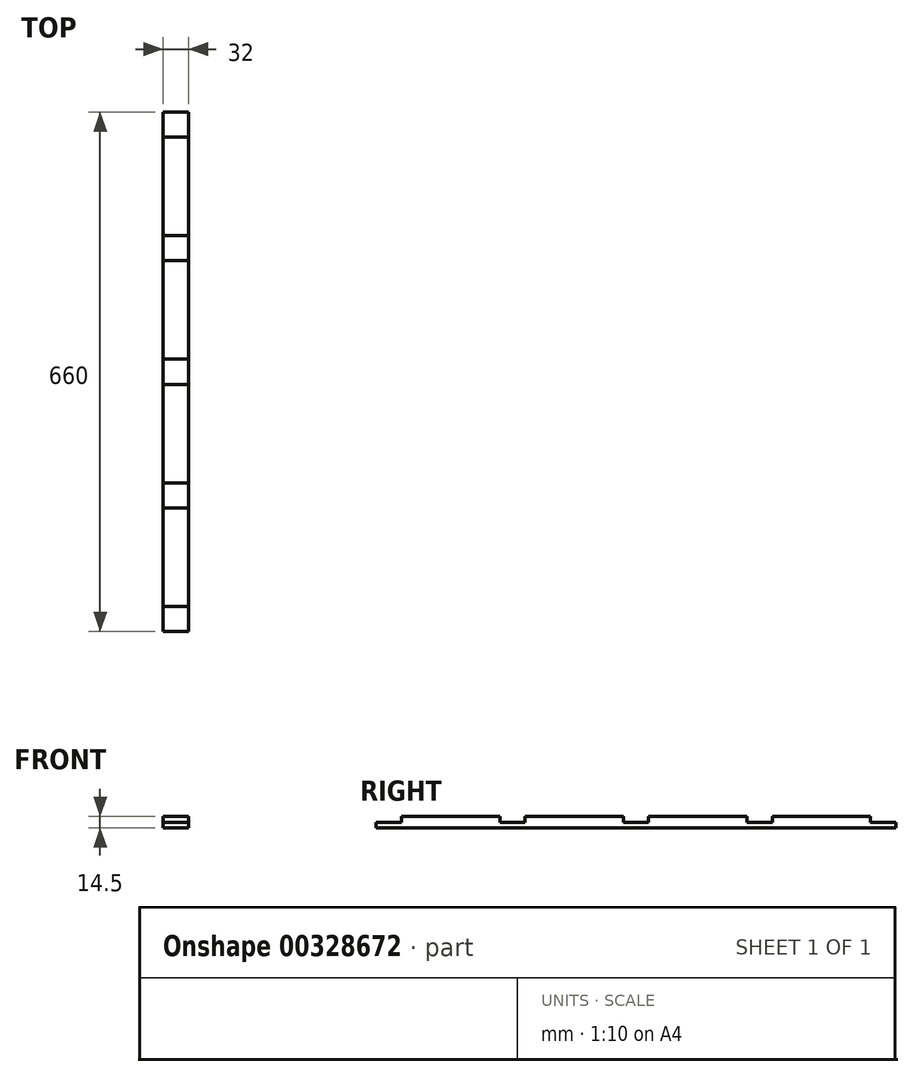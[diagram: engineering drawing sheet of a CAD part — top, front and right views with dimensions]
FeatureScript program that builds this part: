
annotation { "Feature Type Name" : "Feature", "Feature Type Description" : "" }
export const myFeature = defineFeature(function(context is Context, id is Id, definition is map)
    precondition{}
    {
        {
            var Q0;
            Q0=qCreatedBy(makeId("Right.planeOp"),FACE);
            var sketch = newSketch(context, id + "F0", { "sketchPlane" : qUnion([Q0])});
            skLineSegment(sketch, "E0.bottom", {"start": v(0, 0) * mm, "end": v(660, 0) * mm});
            skLineSegment(sketch, "E0.top", {"start": v(32, 14.5) * mm, "end": v(157, 14.5) * mm});
            skLineSegment(sketch, "E0.left", {"start": v(0, 0) * mm, "end": v(0, 7.25) * mm});
            skLineSegment(sketch, "E0.right", {"start": v(660, 0) * mm, "end": v(660, 7.25) * mm});
            skLineSegment(sketch, "E1", {"start": v(0, 7.25) * mm, "end": v(32, 7.25) * mm});
            skLineSegment(sketch, "E2", {"start": v(32, 7.25) * mm, "end": v(32, 14.5) * mm});
            skPoint(sketch, "E3.orphan", {"position": v(0, 14.5) * mm});
            skLineSegment(sketch, "E4", {"start": v(157, 14.5) * mm, "end": v(157, 7.25) * mm});
            skLineSegment(sketch, "E5", {"start": v(157, 7.25) * mm, "end": v(189, 7.25) * mm});
            skLineSegment(sketch, "E6", {"start": v(189, 7.25) * mm, "end": v(189, 14.5) * mm});
            skLineSegment(sketch, "E7.trimOffspring", {"start": v(189, 14.5) * mm, "end": v(314, 14.5) * mm});
            skLineSegment(sketch, "E8", {"start": v(314, 14.5) * mm, "end": v(314, 7.25) * mm});
            skLineSegment(sketch, "E9", {"start": v(314, 7.25) * mm, "end": v(346, 7.25) * mm});
            skLineSegment(sketch, "E10", {"start": v(346, 7.25) * mm, "end": v(346, 14.5) * mm});
            skLineSegment(sketch, "E11.trimOffspring", {"start": v(346, 14.5) * mm, "end": v(471, 14.5) * mm});
            skLineSegment(sketch, "E12", {"start": v(471, 14.5) * mm, "end": v(471, 7.25) * mm});
            skLineSegment(sketch, "E13", {"start": v(471, 7.25) * mm, "end": v(503, 7.25) * mm});
            skLineSegment(sketch, "E14", {"start": v(503, 7.25) * mm, "end": v(503, 14.5) * mm});
            skLineSegment(sketch, "E15.trimOffspring", {"start": v(503, 14.5) * mm, "end": v(628, 14.5) * mm});
            skLineSegment(sketch, "E16", {"start": v(660, 7.25) * mm, "end": v(628, 7.25) * mm});
            skLineSegment(sketch, "E17", {"start": v(628, 7.25) * mm, "end": v(628, 14.5) * mm});
            skPoint(sketch, "E18.orphan", {"position": v(660, 14.5) * mm});
            skSolve(sketch);
        }
        {
            var Q0;
            Q0=qSketchRegion(id+"F0",true);
            extrude(context, id + "F1", {"entities" : qUnion([Q0]), "oppositeDirection" : true, "depth" : 32 * mm});
        }
    });
